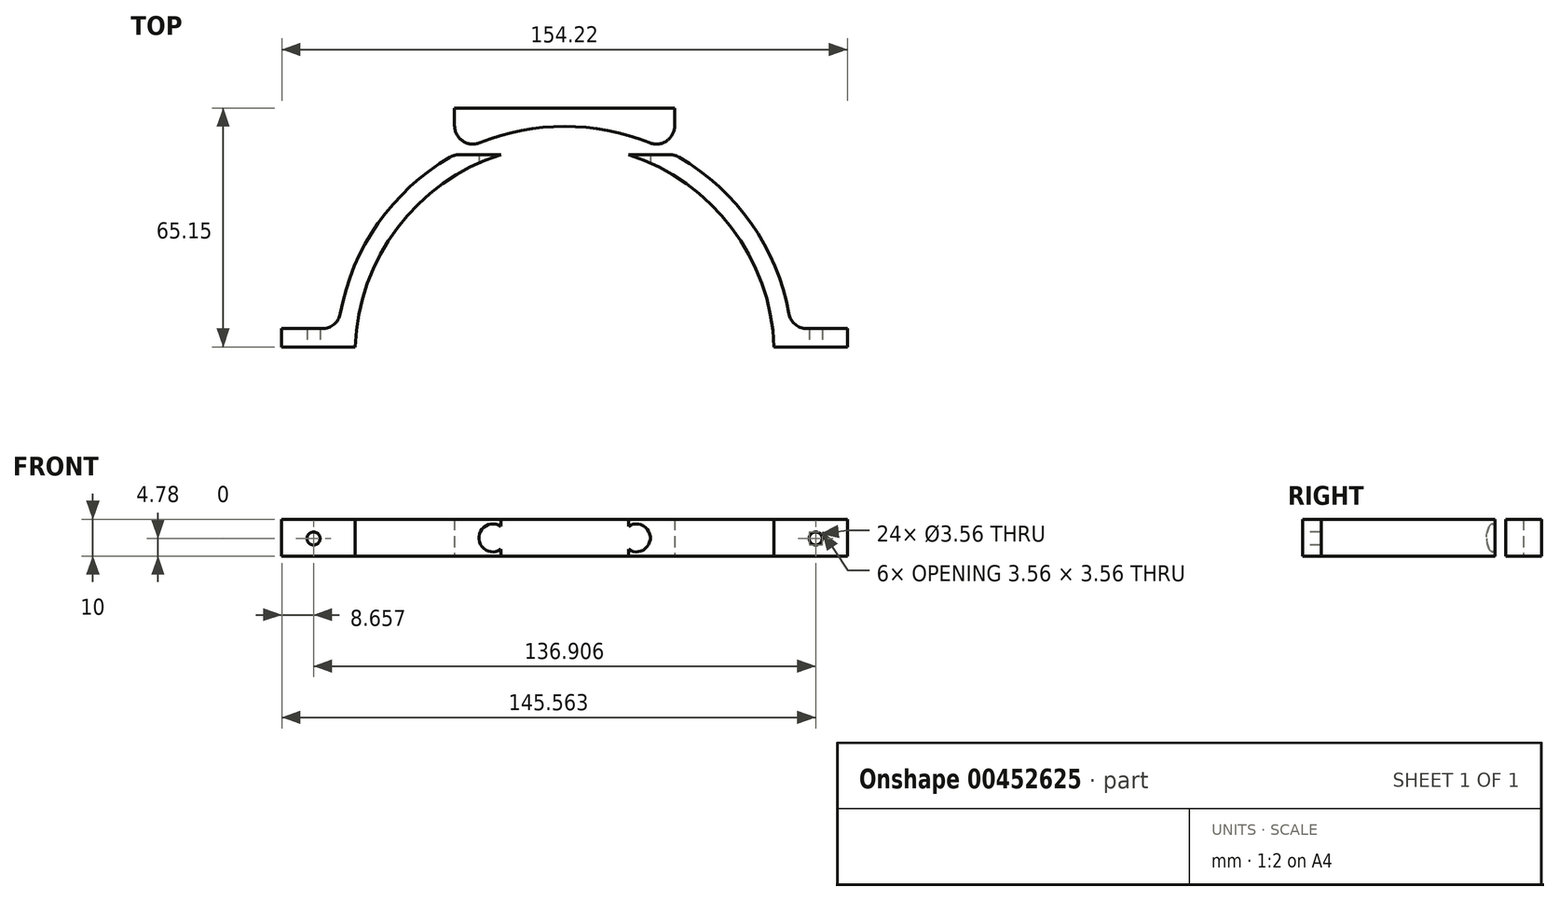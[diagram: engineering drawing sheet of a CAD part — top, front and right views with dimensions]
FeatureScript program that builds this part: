
annotation { "Feature Type Name" : "Feature", "Feature Type Description" : "" }
export const myFeature = defineFeature(function(context is Context, id is Id, definition is map)
    precondition{}
    {
        {
            var Q0;
            Q0=qCreatedBy(makeId("Top.planeOp"),FACE);
            var sketch = newSketch(context, id + "F0", { "sketchPlane" : qUnion([Q0])});
            skCircle(sketch, "E0", {"center": v(0, 0) * mm, "radius": 57.15 * mm, "construction": true});
            skLineSegment(sketch, "E1", {"start": v(-71.53, 0) * mm, "end": v(71.36, 0) * mm, "construction": true});
            skLineSegment(sketch, "E2", {"start": v(-71.7, 2) * mm, "end": v(71.19, 2) * mm, "construction": true});
            skArc(sketch, "E3", {"start": v(57.11, 2) * mm, "mid": v(0, 57.15) * mm, "end": v(-57.11, 2) * mm});
            skArc(sketch, "E4", {"start": v(62.12, 2) * mm, "mid": v(0, 62.15) * mm, "end": v(-62.12, 2) * mm});
            skLineSegment(sketch, "E5", {"start": v(-62.12, 2) * mm, "end": v(-57.11, 2) * mm});
            skLineSegment(sketch, "E6", {"start": v(57.11, 2) * mm, "end": v(62.12, 2) * mm});
            skLineSegment(sketch, "E7.bottom", {"start": v(-57.11, 2) * mm, "end": v(-77.11, 2) * mm});
            skLineSegment(sketch, "E7.top", {"start": v(-57.11, 7) * mm, "end": v(-77.11, 7) * mm});
            skLineSegment(sketch, "E7.left", {"start": v(-57.11, 2) * mm, "end": v(-57.11, 7) * mm});
            skLineSegment(sketch, "E7.right", {"start": v(-77.11, 2) * mm, "end": v(-77.11, 7) * mm});
            skLineSegment(sketch, "E8.bottom", {"start": v(57.11, 2) * mm, "end": v(77.11, 2) * mm});
            skLineSegment(sketch, "E8.top", {"start": v(57.11, 7) * mm, "end": v(77.11, 7) * mm});
            skLineSegment(sketch, "E8.left", {"start": v(57.11, 2) * mm, "end": v(57.11, 7) * mm});
            skLineSegment(sketch, "E8.right", {"start": v(77.11, 2) * mm, "end": v(77.11, 7) * mm});
            skLineSegment(sketch, "E9.bottom", {"start": v(-30, 62.15) * mm, "end": v(30, 62.15) * mm});
            skLineSegment(sketch, "E9.top", {"start": v(-30, 54.43) * mm, "end": v(30, 54.43) * mm});
            skLineSegment(sketch, "E9.left", {"start": v(-30, 62.15) * mm, "end": v(-30, 54.43) * mm});
            skLineSegment(sketch, "E9.right", {"start": v(30, 62.15) * mm, "end": v(30, 54.43) * mm});
            skPoint(sketch, "E10", {"position": v(0, 62.15) * mm});
            skLineSegment(sketch, "E11.top", {"start": v(-30, 48.64) * mm, "end": v(30, 48.64) * mm});
            skLineSegment(sketch, "E11.left", {"start": v(-30, 54.43) * mm, "end": v(-30, 48.64) * mm});
            skLineSegment(sketch, "E11.right", {"start": v(30, 54.43) * mm, "end": v(30, 48.64) * mm});
            skLineSegment(sketch, "E12.top", {"start": v(-30, 67.15) * mm, "end": v(30, 67.15) * mm});
            skLineSegment(sketch, "E12.left", {"start": v(-30, 62.15) * mm, "end": v(-30, 67.15) * mm});
            skLineSegment(sketch, "E12.right", {"start": v(30, 62.15) * mm, "end": v(30, 67.15) * mm});
            skSolve(sketch);
        }
        {
            var Q0;
            Q0=makeQuery(id+"F0.imprint","IMPRINT",FACE,{"disambiguationData":[TD([[makeQuery(id+"F0.imprint","IMPRINT",EDGE,{"derivedFrom":sQuery(id+"F0.wireOp",EDGE,"E3")}),-1.0]])]});
            var Q1;
            {var subQ5=sQuery(id+"F0.wireOp",EDGE,"E7.right");Q1=makeQuery(id+"F0.imprint","IMPRINT",FACE,{"disambiguationData":[TD([[makeQuery(id+"F0.imprint","IMPRINT",EDGE,{"derivedFrom":subQ5}),-1.0]])]});}
            var Q2;
            {var subQ5=sQuery(id+"F0.wireOp",EDGE,"E7.left");Q2=makeQuery(id+"F0.imprint","IMPRINT",FACE,{"disambiguationData":[TD([[makeQuery(id+"F0.imprint","IMPRINT",EDGE,{"derivedFrom":subQ5}),1.0]])]});}
            var Q3;
            {var subQ5=sQuery(id+"F0.wireOp",EDGE,"E8.left");Q3=makeQuery(id+"F0.imprint","IMPRINT",FACE,{"disambiguationData":[TD([[makeQuery(id+"F0.imprint","IMPRINT",EDGE,{"derivedFrom":subQ5}),-1.0]])]});}
            var Q4;
            {var subQ5=sQuery(id+"F0.wireOp",EDGE,"E8.right");Q4=makeQuery(id+"F0.imprint","IMPRINT",FACE,{"disambiguationData":[TD([[makeQuery(id+"F0.imprint","IMPRINT",EDGE,{"derivedFrom":subQ5}),1.0]])]});}
            var Q5;
            {var subQ0=sQuery(id+"F0.wireOp",EDGE,"E9.left");Q5=makeQuery(id+"F0.imprint","IMPRINT",FACE,{"disambiguationData":[TD([[makeQuery(id+"F0.imprint","IMPRINT",EDGE,{"derivedFrom":subQ0}),1.0]])]});}
            var Q6;
            {var subQ0=sQuery(id+"F0.wireOp",EDGE,"E9.right");Q6=makeQuery(id+"F0.imprint","IMPRINT",FACE,{"disambiguationData":[TD([[makeQuery(id+"F0.imprint","IMPRINT",EDGE,{"derivedFrom":subQ0}),-1.0]])]});}
            var Q7;
            {var subQ0=sQuery(id+"F0.wireOp",EDGE,"E7.left");Q7=makeQuery(id+"F0.imprint","IMPRINT",FACE,{"disambiguationData":[TD([[makeQuery(id+"F0.imprint","IMPRINT",EDGE,{"derivedFrom":subQ0}),-1.0]])]});}
            var Q8;
            {var subQ0=sQuery(id+"F0.wireOp",EDGE,"E9.top");var subQ4=sQuery(id+"F0.wireOp",EDGE,"E3");var subQ7=makeQuery(id+"F0.imprint","INTERSECT",VERTEX,{"disambiguationData":[OD(0.0)],"derivedFrom":[subQ4,subQ0]});Q8=makeQuery(id+"F0.imprint","IMPRINT",FACE,{"disambiguationData":[TD([[makeQuery(id+"F0.imprint","IMPRINT",EDGE,{"disambiguationData":[TD([[subQ7,-1.0]])],"derivedFrom":subQ4}),-1.0]])]});}
            var Q9;
            {var subQ0=sQuery(id+"F0.wireOp",EDGE,"E11.top");Q9=makeQuery(id+"F0.imprint","IMPRINT",FACE,{"disambiguationData":[TD([[makeQuery(id+"F0.imprint","IMPRINT",EDGE,{"derivedFrom":subQ0}),1.0]])]});}
            var Q10;
            {var subQ0=sQuery(id+"F0.wireOp",EDGE,"E8.left");Q10=makeQuery(id+"F0.imprint","IMPRINT",FACE,{"disambiguationData":[TD([[makeQuery(id+"F0.imprint","IMPRINT",EDGE,{"derivedFrom":subQ0}),1.0]])]});}
            var Q11;
            Q11=makeQuery(id+"F0.imprint","IMPRINT",FACE,{"disambiguationData":[TD([[makeQuery(id+"F0.imprint","IMPRINT",EDGE,{"derivedFrom":sQuery(id+"F0.wireOp",EDGE,"E12.top")}),-1.0]])]});
            extrude(context, id + "F1", {"entities" : qUnion([Q0, Q1, Q2, Q3, Q4, Q5, Q6, Q7, Q8, Q9, Q10, Q11]), "depth" : 10 * mm});
        }
        {
            var Q0;
            Q0=makeQuery(id+"F1.opExtrude","SWEPT_FACE",FACE,{"disambiguationData":[OSD([sQuery(id+"F0.wireOp",EDGE,"E11.top")])]});
            var sketch = newSketch(context, id + "F2", { "sketchPlane" : qUnion([Q0])});
            skPoint(sketch, "E13", {"position": v(-19.56, 4.95) * mm});
            skPoint(sketch, "E14.MirrorP", {"position": v(19.56, 4.95) * mm});
            skSolve(sketch);
        }
        {
            var Q0;
            Q0=sQuery(id+"F2.wireOp",VERTEX,"E13");
            var Q1;
            Q1=sQuery(id+"F2.wireOp",VERTEX,"E14.MirrorP");
            var Q2;
            Q2=makeQuery(id+"F1.opExtrude","SWEPT_BODY",BODY,{"disambiguationData":[OSD([sQuery(id+"F0.wireOp",EDGE,"E3"),sQuery(id+"F0.wireOp",EDGE,"E4"),sQuery(id+"F0.wireOp",EDGE,"E7.bottom"),sQuery(id+"F0.wireOp",EDGE,"E7.top"),sQuery(id+"F0.wireOp",EDGE,"E7.right"),sQuery(id+"F0.wireOp",EDGE,"E8.bottom"),sQuery(id+"F0.wireOp",EDGE,"E8.top"),sQuery(id+"F0.wireOp",EDGE,"E8.right"),sQuery(id+"F0.wireOp",EDGE,"E9.bottom"),sQuery(id+"F0.wireOp",EDGE,"E9.left"),sQuery(id+"F0.wireOp",EDGE,"E9.right"),sQuery(id+"F0.wireOp",EDGE,"E9.top"),sQuery(id+"F0.wireOp",EDGE,"E11.top")])]});
            hole(context, id + "F3", {"style" : HoleStyle.C_BORE, "endStyle" : HoleEndStyle.THROUGH, "holeDiameter" : 3.56 * mm, "cBoreDiameter" : 7.62 * mm, "cBoreDepth" : 10 * mm, "isTappedThrough" : true, "tappedDepth" : 12 * mm, "tapClearance" : 3, "locations" : qUnion([Q0, Q1]), "scope" : qUnion([Q2])});
        }
        {
            var Q0;
            {var subQ0=sQuery(id+"F0.wireOp",EDGE,"E11.top");Q0=makeQuery(id+"F0.imprint","IMPRINT",FACE,{"disambiguationData":[TD([[makeQuery(id+"F0.imprint","IMPRINT",EDGE,{"derivedFrom":subQ0}),1.0]])]});}
            extrude(context, id + "F4", {"entities" : qUnion([Q0]), "operationType" : NewBodyOperationType.REMOVE, "endBound" : BoundingType.THROUGH_ALL, "depth" : 25 * mm});
        }
        {
            var Q0;
            Q0=makeQuery(id+"F1.opExtrude","SWEPT_FACE",FACE,{"disambiguationData":[OSD([sQuery(id+"F0.wireOp",EDGE,"E7.bottom")])]});
            var sketch = newSketch(context, id + "F5", { "sketchPlane" : qUnion([Q0])});
            skPoint(sketch, "E15", {"position": v(-68.45, 4.78) * mm});
            skPoint(sketch, "E16.MirrorP", {"position": v(68.45, 4.78) * mm});
            skSolve(sketch);
        }
        {
            var Q0;
            Q0=sQuery(id+"F5.wireOp",VERTEX,"E15");
            var Q1;
            Q1=sQuery(id+"F5.wireOp",VERTEX,"E16.MirrorP");
            var Q2;
            Q2=makeQuery(id+"F1.opExtrude","SWEPT_BODY",BODY,{"disambiguationData":[OSD([sQuery(id+"F0.wireOp",EDGE,"E3"),sQuery(id+"F0.wireOp",EDGE,"E4"),sQuery(id+"F0.wireOp",EDGE,"E7.bottom"),sQuery(id+"F0.wireOp",EDGE,"E7.top"),sQuery(id+"F0.wireOp",EDGE,"E7.right"),sQuery(id+"F0.wireOp",EDGE,"E8.bottom"),sQuery(id+"F0.wireOp",EDGE,"E8.top"),sQuery(id+"F0.wireOp",EDGE,"E8.right"),sQuery(id+"F0.wireOp",EDGE,"E9.left"),sQuery(id+"F0.wireOp",EDGE,"E9.right"),sQuery(id+"F0.wireOp",EDGE,"E9.top"),sQuery(id+"F0.wireOp",EDGE,"E11.top"),sQuery(id+"F0.wireOp",EDGE,"E12.top"),sQuery(id+"F0.wireOp",EDGE,"E12.left"),sQuery(id+"F0.wireOp",EDGE,"E12.right")])]});
            hole(context, id + "F6", {"style" : HoleStyle.SIMPLE, "endStyle" : HoleEndStyle.THROUGH, "holeDiameter" : 3.56 * mm, "isTappedThrough" : true, "tappedDepth" : 12 * mm, "tapClearance" : 3, "locations" : qUnion([Q0, Q1]), "scope" : qUnion([Q2])});
        }
        {
            var Q0;
            Q0=makeQuery(id+"F1.opExtrude","SWEPT_EDGE",EDGE,{"disambiguationData":[OSD([sQuery(id+"F0.wireOp",EDGE,"E4"),sQuery(id+"F0.wireOp",EDGE,"E7.top")])]});
            var Q1;
            Q1=makeQuery(id+"F1.opExtrude","SWEPT_EDGE",EDGE,{"disambiguationData":[OSD([sQuery(id+"F0.wireOp",EDGE,"E4"),sQuery(id+"F0.wireOp",EDGE,"E8.top")])]});
            var Q2;
            Q2=makeQuery(id+"F1.opExtrude","SWEPT_EDGE",EDGE,{"disambiguationData":[OSD([sQuery(id+"F0.wireOp",EDGE,"E4"),sQuery(id+"F0.wireOp",EDGE,"E9.right"),sQuery(id+"F0.wireOp",EDGE,"E9.top"),sQuery(id+"F0.wireOp",EDGE,"E11.right")])]});
            var Q3;
            Q3=makeQuery(id+"F1.opExtrude","SWEPT_EDGE",EDGE,{"disambiguationData":[OSD([sQuery(id+"F0.wireOp",EDGE,"E4"),sQuery(id+"F0.wireOp",EDGE,"E9.left"),sQuery(id+"F0.wireOp",EDGE,"E9.top"),sQuery(id+"F0.wireOp",EDGE,"E11.left")])]});
            fillet(context, id + "F7", {"entities" : qUnion([Q0, Q1, Q2, Q3]), "radius" : 5 * mm, "tangentPropagation" : true, "allowEdgeOverflow" : false});
        }
    });
